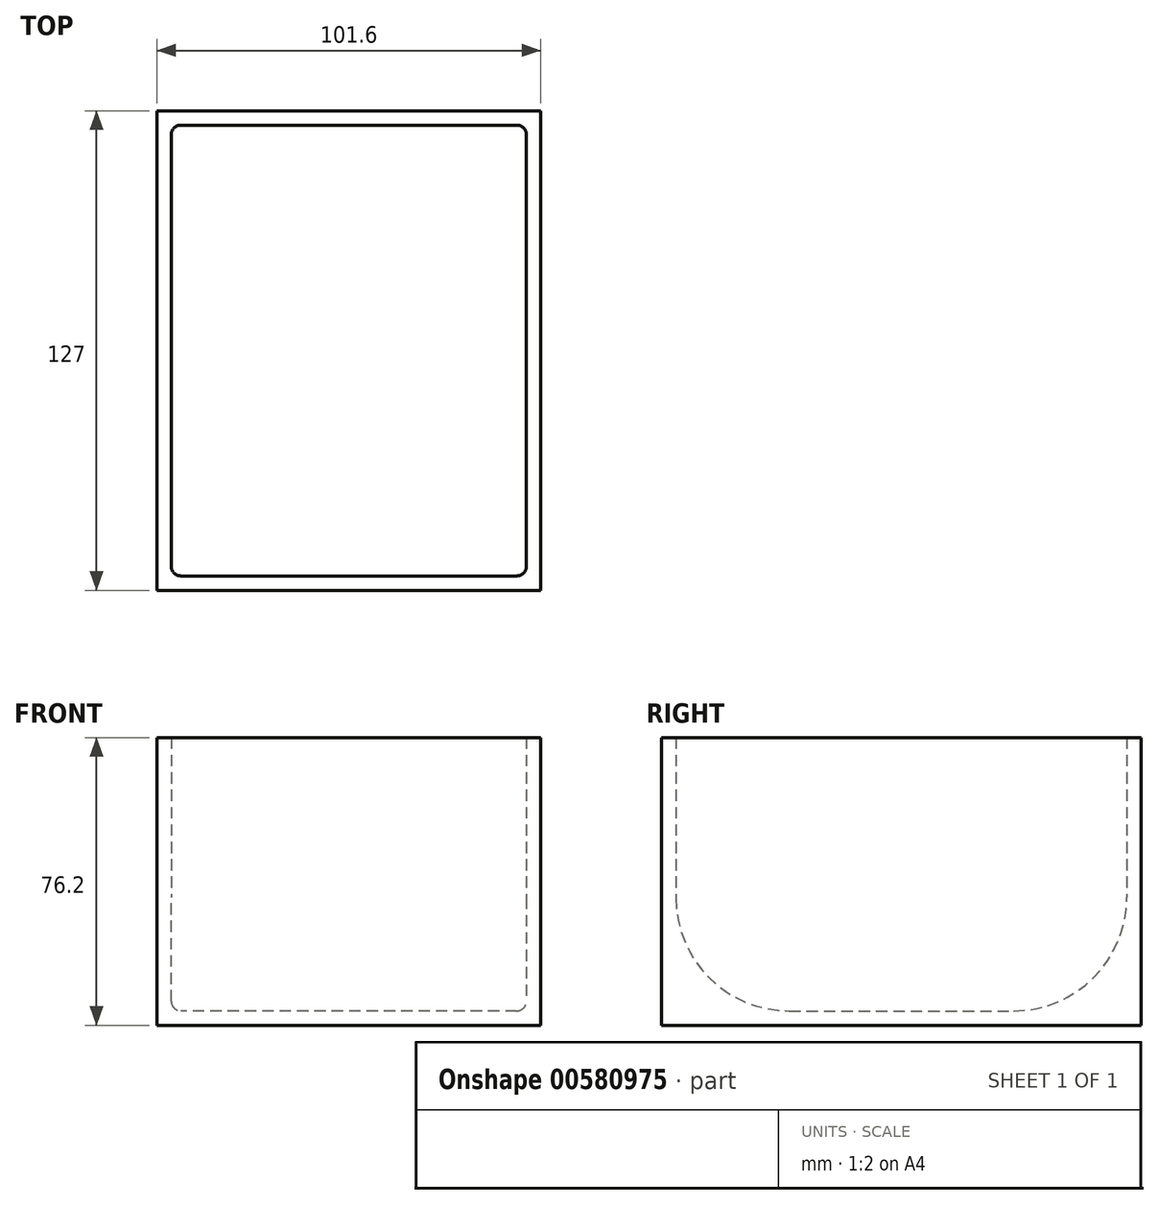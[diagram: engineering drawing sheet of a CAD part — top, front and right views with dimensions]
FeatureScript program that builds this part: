
annotation { "Feature Type Name" : "Feature", "Feature Type Description" : "" }
export const myFeature = defineFeature(function(context is Context, id is Id, definition is map)
    precondition{}
    {
        {
            var Q0;
            Q0=qCreatedBy(makeId("Top.planeOp"),FACE);
            var sketch = newSketch(context, id + "F0", { "sketchPlane" : qUnion([Q0])});
            skLineSegment(sketch, "E0.bottom", {"start": v(50.8, -63.5) * mm, "end": v(-50.8, -63.5) * mm});
            skLineSegment(sketch, "E0.top", {"start": v(50.8, 63.5) * mm, "end": v(-50.8, 63.5) * mm});
            skLineSegment(sketch, "E0.left", {"start": v(50.8, -63.5) * mm, "end": v(50.8, 63.5) * mm});
            skLineSegment(sketch, "E0.right", {"start": v(-50.8, -63.5) * mm, "end": v(-50.8, 63.5) * mm});
            skPoint(sketch, "E0.middle", {"position": v(0, 0) * mm});
            skSolve(sketch);
        }
        {
            var Q0;
            Q0=makeQuery(id+"F0.imprint","IMPRINT",FACE,{"disambiguationData":[TD([[makeQuery(id+"F0.imprint","IMPRINT",EDGE,{"derivedFrom":sQuery(id+"F0.wireOp",EDGE,"E0.bottom")}),-1.0]])]});
            extrude(context, id + "F1", {"entities" : qUnion([Q0]), "depth" : 76.2 * mm, "offsetDistance" : 25 * mm});
        }
        {
            var Q0;
            Q0=makeQuery(id+"F1.opExtrude","CAP_FACE",FACE,{"disambiguationData":[OSD([sQuery(id+"F0.wireOp",EDGE,"E0.bottom"),sQuery(id+"F0.wireOp",EDGE,"E0.top"),sQuery(id+"F0.wireOp",EDGE,"E0.left"),sQuery(id+"F0.wireOp",EDGE,"E0.right")])],"isStart":false});
            shell(context, id + "F2", {"entities" : qUnion([Q0]), "thickness" : 3.8 * mm});
        }
        {
            var Q0;
            {var subQ0=sQuery(id+"F0.wireOp",EDGE,"E0.top");Q0=makeQuery(id+"F2.opShell","OFFSET_EDGE",EDGE,{"disambiguationData":[OSD([subQ0]),TDD([makeQuery(id+"F1.opExtrude","CAP_EDGE",EDGE,{"disambiguationData":[OSD([subQ0])],"isStart":true})])]});}
            var Q1;
            {var subQ0=sQuery(id+"F0.wireOp",EDGE,"E0.bottom");Q1=makeQuery(id+"F2.opShell","OFFSET_EDGE",EDGE,{"disambiguationData":[OSD([subQ0]),TDD([makeQuery(id+"F1.opExtrude","CAP_EDGE",EDGE,{"disambiguationData":[OSD([subQ0])],"isStart":true})])]});}
            fillet(context, id + "F3", {"entities" : qUnion([Q0, Q1]), "radius" : 30 * mm, "tangentPropagation" : true, "allowEdgeOverflow" : false});
        }
        {
            var Q0;
            {var subQ0=sQuery(id+"F0.wireOp",EDGE,"E0.bottom");Q0=makeQuery(id+"F3.opFillet","BLEND_EDGE",EDGE,{"blendedFrom":[makeQuery(id+"F2.opShell","OFFSET_EDGE",EDGE,{"disambiguationData":[OSD([subQ0]),TDD([makeQuery(id+"F1.opExtrude","CAP_EDGE",EDGE,{"disambiguationData":[OSD([subQ0])],"isStart":true})])]}),makeQuery(id+"F2.opShell","OFFSET_FACE",FACE,{"disambiguationData":[OSD([sQuery(id+"F0.wireOp",EDGE,"E0.right")])]})],"blendedInto":[makeQuery(id+"F2.opShell","OFFSET_FACE",FACE,{"disambiguationData":[OSD([sQuery(id+"F0.wireOp",EDGE,"E0.right")])]})]});}
            var Q1;
            {var subQ0=sQuery(id+"F0.wireOp",EDGE,"E0.bottom");Q1=makeQuery(id+"F3.opFillet","BLEND_EDGE",EDGE,{"blendedFrom":[makeQuery(id+"F2.opShell","OFFSET_EDGE",EDGE,{"disambiguationData":[OSD([subQ0]),TDD([makeQuery(id+"F1.opExtrude","CAP_EDGE",EDGE,{"disambiguationData":[OSD([subQ0])],"isStart":true})])]}),makeQuery(id+"F2.opShell","OFFSET_FACE",FACE,{"disambiguationData":[OSD([sQuery(id+"F0.wireOp",EDGE,"E0.left")])]})],"blendedInto":[makeQuery(id+"F2.opShell","OFFSET_FACE",FACE,{"disambiguationData":[OSD([sQuery(id+"F0.wireOp",EDGE,"E0.left")])]})]});}
            fillet(context, id + "F4", {"entities" : qUnion([Q0, Q1]), "radius" : 2.5 * mm, "tangentPropagation" : true, "allowEdgeOverflow" : false});
        }
        {
            var Q0;
            Q0=makeQuery(id+"F1.opExtrude","CAP_FACE",FACE,{"disambiguationData":[OSD([sQuery(id+"F0.wireOp",EDGE,"E0.bottom"),sQuery(id+"F0.wireOp",EDGE,"E0.top"),sQuery(id+"F0.wireOp",EDGE,"E0.left"),sQuery(id+"F0.wireOp",EDGE,"E0.right")])],"isStart":false});
            extrude(context, id + "F5", {"entities" : qUnion([Q0]), "operationType" : NewBodyOperationType.ADD, "oppositeDirection" : true, "depth" : 76.2 * mm, "offsetDistance" : 25 * mm});
        }
    });
